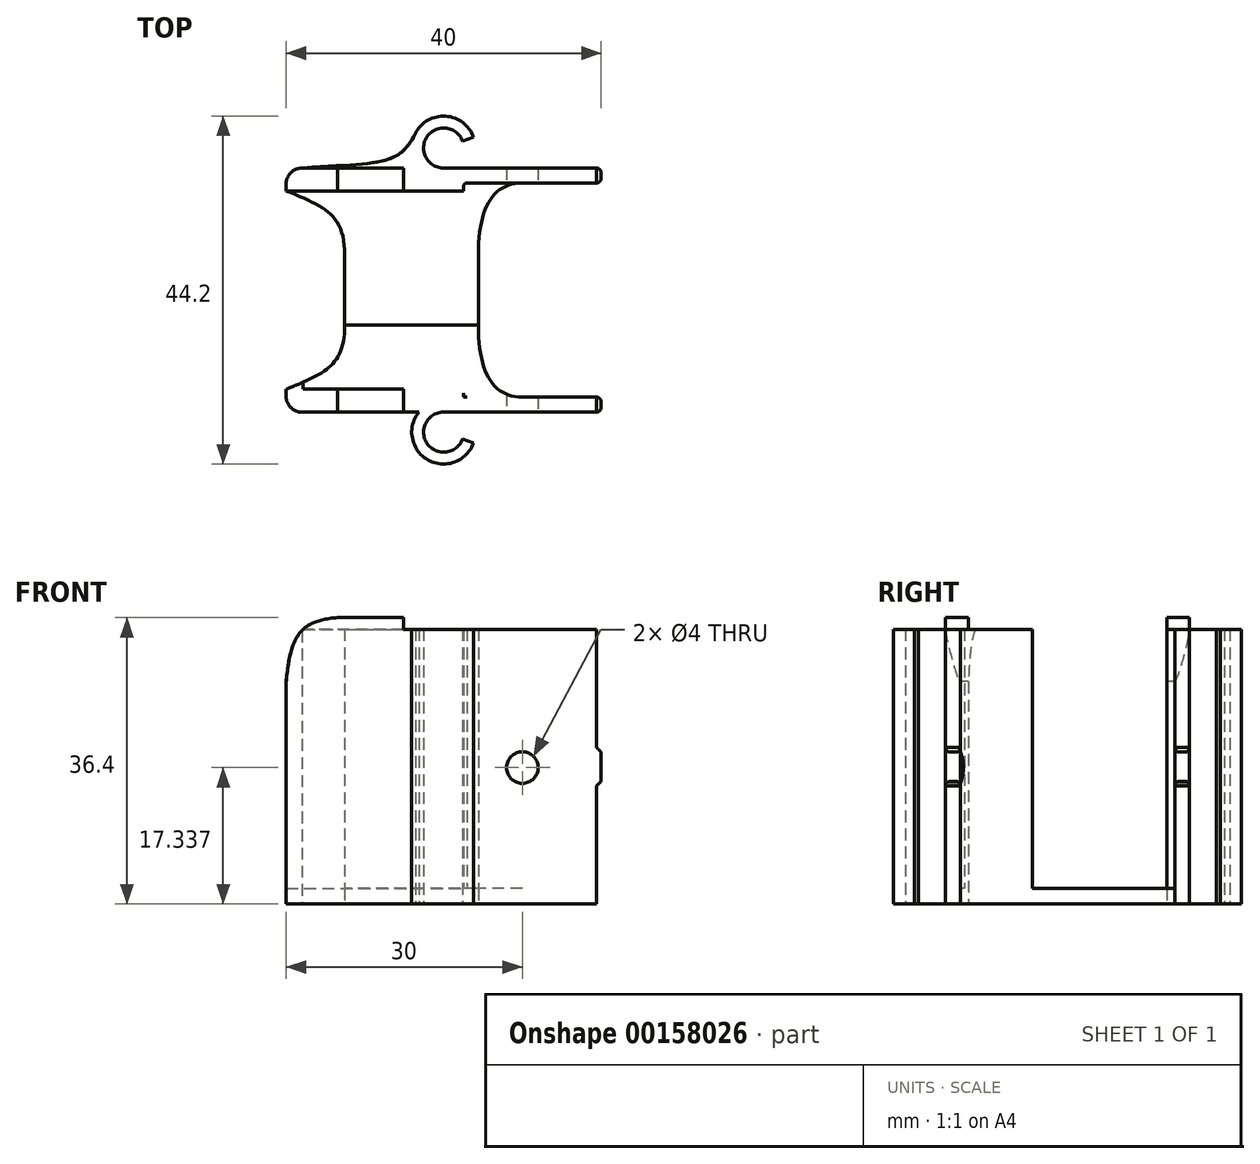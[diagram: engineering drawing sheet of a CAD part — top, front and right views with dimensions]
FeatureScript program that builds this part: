
annotation { "Feature Type Name" : "Feature", "Feature Type Description" : "" }
export const myFeature = defineFeature(function(context is Context, id is Id, definition is map)
    precondition{}
    {
        {
            var Q0;
            Q0=qCreatedBy(makeId("Top.planeOp"),FACE);
            var sketch = newSketch(context, id + "F0", { "sketchPlane" : qUnion([Q0])});
            skCircle(sketch, "E0", {"center": v(0, 18.05) * mm, "radius": 2.55 * mm});
            skCircle(sketch, "E1", {"center": v(0, 18.05) * mm, "radius": 4.05 * mm});
            skLineSegment(sketch, "E2", {"start": v(-20, 12.6) * mm, "end": v(2.5, 12.6) * mm});
            skLineSegment(sketch, "E3", {"start": v(19.4, 15.5) * mm, "end": v(-18, 15.5) * mm});
            skLineSegment(sketch, "E4", {"start": v(-20, 13.5) * mm, "end": v(-20, 12.6) * mm});
            skLineSegment(sketch, "E5", {"start": v(-43.37, 0) * mm, "end": v(27.82, 0) * mm, "construction": true});
            skLineSegment(sketch, "E6", {"start": v(10, 20.96) * mm, "end": v(10, -7.85) * mm, "construction": true});
            skLineSegment(sketch, "E7", {"start": v(0, 18.05) * mm, "end": v(11.1, 22.1) * mm});
            skLineSegment(sketch, "E8", {"start": v(14.32, 18.05) * mm, "end": v(-31, 18.05) * mm, "construction": true});
            skLineSegment(sketch, "E9", {"start": v(20, 14.9) * mm, "end": v(20, 14.2) * mm});
            skLineSegment(sketch, "E10", {"start": v(19.4, 13.6) * mm, "end": v(3, 13.6) * mm});
            skLineSegment(sketch, "E11", {"start": v(2.5, 12.6) * mm, "end": v(2.5, 13.1) * mm});
            skPoint(sketch, "E12.visualSharp", {"position": v(20, 15.5) * mm});
            skArc(sketch, "E12.filletArc", {"start": v(20, 14.9) * mm, "mid": v(19.82, 15.32) * mm, "end": v(19.4, 15.5) * mm});
            skPoint(sketch, "E13.visualSharp", {"position": v(20, 13.6) * mm});
            skArc(sketch, "E13.filletArc", {"start": v(19.4, 13.6) * mm, "mid": v(19.82, 13.78) * mm, "end": v(20, 14.2) * mm});
            skPoint(sketch, "E14.visualSharp", {"position": v(-20, 15.5) * mm});
            skArc(sketch, "E14.filletArc", {"start": v(-18, 15.5) * mm, "mid": v(-19.41, 14.91) * mm, "end": v(-20, 13.5) * mm});
            skLineSegment(sketch, "E15.bottom", {"start": v(-12.56, 0) * mm, "end": v(4.4, 0) * mm});
            skLineSegment(sketch, "E15.top", {"start": v(-12.56, 4.46) * mm, "end": v(4.4, 4.46) * mm});
            skLineSegment(sketch, "E15.left", {"start": v(-12.56, 0) * mm, "end": v(-12.56, 4.46) * mm});
            skLineSegment(sketch, "E15.right", {"start": v(4.4, 0) * mm, "end": v(4.4, 4.46) * mm});
            skLineSegment(sketch, "E16.MirrorCS", {"start": v(20, -14.9) * mm, "end": v(20, -14.2) * mm});
            skArc(sketch, "E17.MirrorCS", {"start": v(19.4, -13.6) * mm, "mid": v(19.82, -13.78) * mm, "end": v(20, -14.2) * mm});
            skArc(sketch, "E18.MirrorCS", {"start": v(20, -14.9) * mm, "mid": v(19.82, -15.32) * mm, "end": v(19.4, -15.5) * mm});
            skLineSegment(sketch, "E19.MirrorCS", {"start": v(2.5, -12.6) * mm, "end": v(2.5, -13.6) * mm});
            skLineSegment(sketch, "E20.MirrorCS", {"start": v(-20, -13.5) * mm, "end": v(-20, -12.6) * mm});
            skArc(sketch, "E21.MirrorCS", {"start": v(-18, -15.5) * mm, "mid": v(-19.41, -14.91) * mm, "end": v(-20, -13.5) * mm});
            skPoint(sketch, "E22.MirrorP", {"position": v(20, -15.5) * mm});
            skLineSegment(sketch, "E23.MirrorCS", {"start": v(19.4, -13.6) * mm, "end": v(2.5, -13.6) * mm});
            skLineSegment(sketch, "E24.MirrorCS", {"start": v(19.4, -15.5) * mm, "end": v(-18, -15.5) * mm});
            skLineSegment(sketch, "E25.MirrorCS", {"start": v(-20, -12.6) * mm, "end": v(2.5, -12.6) * mm});
            skPoint(sketch, "E26.MirrorP", {"position": v(20, -13.6) * mm});
            skCircle(sketch, "E27.MirrorC", {"center": v(0, -18.05) * mm, "radius": 4.05 * mm});
            skCircle(sketch, "E28.MirrorC", {"center": v(0, -18.05) * mm, "radius": 2.55 * mm});
            skPoint(sketch, "E29.MirrorP", {"position": v(-20, -15.5) * mm});
            skLineSegment(sketch, "E30.MirrorCS", {"start": v(-12.56, -4.46) * mm, "end": v(4.4, -4.46) * mm});
            skLineSegment(sketch, "E31.MirrorCS", {"start": v(-12.56, 0) * mm, "end": v(-12.56, -4.46) * mm});
            skLineSegment(sketch, "E32.MirrorCS", {"start": v(4.4, 0) * mm, "end": v(4.4, -4.46) * mm});
            skLineSegment(sketch, "E33.MirrorCS", {"start": v(0, -18.05) * mm, "end": v(11.1, -22.1) * mm});
            skFitSpline(sketch, "E34", {"points": [v(10, 13.6) * mm, v(4.4, 4.46) * mm], "startDerivative": vector(-11.27, 0) * mm, "endDerivative": vector(0, -18.1) * mm});
            skFitSpline(sketch, "E35", {"points": [v(-20, 12.6) * mm, v(-12.56, 4.46) * mm], "startDerivative": vector(13.93, -5.77) * mm, "endDerivative": vector(0, -15.8) * mm});
            skFitSpline(sketch, "E36.MirrorCS", {"points": [v(10, -13.6) * mm, v(4.4, -4.46) * mm], "startDerivative": vector(-11.27, 0) * mm, "endDerivative": vector(0, 18.1) * mm});
            skFitSpline(sketch, "E37.MirrorCS", {"points": [v(-20, -12.6) * mm, v(-12.56, -4.46) * mm], "startDerivative": vector(13.93, 5.77) * mm, "endDerivative": vector(0, 15.8) * mm});
            skPoint(sketch, "E38", {"position": v(-8.34, 18.05) * mm});
            skFitSpline(sketch, "E39", {"points": [v(-18, 15.5) * mm, v(-3.59, 19.93) * mm], "startDerivative": vector(27.98, 2.16) * mm, "endDerivative": vector(6.23, 13.18) * mm});
            skPoint(sketch, "E40.visualSharp", {"position": v(2.5, 13.6) * mm});
            skArc(sketch, "E40.filletArc", {"start": v(3, 13.6) * mm, "mid": v(2.65, 13.45) * mm, "end": v(2.5, 13.1) * mm});
            skArc(sketch, "E41.MirrorCS", {"start": v(3, -13.6) * mm, "mid": v(2.65, -13.45) * mm, "end": v(2.5, -13.1) * mm});
            skFitSpline(sketch, "E42.MirrorCS", {"points": [v(-18, -15.5) * mm, v(-3.59, -19.93) * mm], "startDerivative": vector(27.98, -2.16) * mm, "endDerivative": vector(6.23, -13.18) * mm});
            skLineSegment(sketch, "E43", {"start": v(-5.1, -15.5) * mm, "end": v(-5.1, -12.6) * mm});
            skLineSegment(sketch, "E44.MirrorCS", {"start": v(-5.1, 15.5) * mm, "end": v(-5.1, 12.6) * mm});
            skSolve(sketch);
        }
        {
            var Q0;
            Q0=makeQuery(id+"F0.imprint","IMPRINT",FACE,{"disambiguationData":[TD([[makeQuery(id+"F0.imprint","IMPRINT",EDGE,{"derivedFrom":sQuery(id+"F0.wireOp",EDGE,"E2")}),1.0]])]});
            var Q1;
            {var subQ0=sQuery(id+"F0.wireOp",EDGE,"E3");var subQ1=sQuery(id+"F0.wireOp",EDGE,"E1");var subQ2=makeQuery(id+"F0.imprint","INTERSECT",VERTEX,{"disambiguationData":[OD(0.0)],"derivedFrom":[subQ1,subQ0]});Q1=makeQuery(id+"F0.imprint","IMPRINT",FACE,{"disambiguationData":[TD([[makeQuery(id+"F0.imprint","IMPRINT",EDGE,{"disambiguationData":[TD([[subQ2,1.0]])],"derivedFrom":subQ1}),1.0]])]});}
            var Q2;
            Q2=makeQuery(id+"F0.imprint","IMPRINT",FACE,{"disambiguationData":[TD([[makeQuery(id+"F0.imprint","IMPRINT",EDGE,{"derivedFrom":sQuery(id+"F0.wireOp",EDGE,"E9")}),-1.0]])]});
            extrude(context, id + "F1", {"entities" : qUnion([Q0, Q1, Q2]), "depth" : 34.9 * mm});
        }
        {
            var Q0;
            Q0=makeQuery(id+"F0.imprint","IMPRINT",FACE,{"disambiguationData":[TD([[makeQuery(id+"F0.imprint","IMPRINT",EDGE,{"derivedFrom":sQuery(id+"F0.wireOp",EDGE,"E2")}),-1.0]])]});
            var Q1;
            Q1=makeQuery(id+"F0.imprint","IMPRINT",FACE,{"disambiguationData":[TD([[makeQuery(id+"F0.imprint","IMPRINT",EDGE,{"derivedFrom":sQuery(id+"F0.wireOp",EDGE,"E15.bottom")}),1.0]])]});
            var Q2;
            Q2=makeQuery(id+"F0.imprint","IMPRINT",FACE,{"disambiguationData":[TD([[makeQuery(id+"F0.imprint","IMPRINT",EDGE,{"derivedFrom":sQuery(id+"F0.wireOp",EDGE,"E15.bottom")}),-1.0]])]});
            var Q3;
            Q3=makeQuery(id+"F0.imprint","IMPRINT",FACE,{"disambiguationData":[TD([[makeQuery(id+"F0.imprint","IMPRINT",EDGE,{"derivedFrom":sQuery(id+"F0.wireOp",EDGE,"b0b9aed6-4291-49e0-8eb1-d7c1ce640f5c6.MirrorCS")}),1.0]])]});
            var Q4;
            {var subQ1=sQuery(id+"F0.wireOp",EDGE,"E19.MirrorCS");Q4=makeQuery(id+"F0.imprint","IMPRINT",FACE,{"disambiguationData":[TD([[makeQuery(id+"F0.imprint","IMPRINT",EDGE,{"derivedFrom":subQ1}),1.0]])]});}
            var Q5;
            {var subQ3=sQuery(id+"F0.wireOp",EDGE,"E25.MirrorCS");Q5=makeQuery(id+"F0.imprint","IMPRINT",FACE,{"disambiguationData":[TD([[makeQuery(id+"F0.imprint","IMPRINT",EDGE,{"derivedFrom":subQ3}),1.0]])]});}
            extrude(context, id + "F2", {"entities" : qUnion([Q0, Q1, Q2, Q3, Q4, Q5]), "operationType" : NewBodyOperationType.ADD, "depth" : 2 * mm});
        }
        {
            var Q0;
            Q0=makeQuery(id+"F0.imprint","IMPRINT",FACE,{"disambiguationData":[TD([[makeQuery(id+"F0.imprint","IMPRINT",EDGE,{"derivedFrom":sQuery(id+"F0.wireOp",EDGE,"E16.MirrorCS")}),1.0]])]});
            var Q1;
            {var subQ0=sQuery(id+"F0.wireOp",EDGE,"E27.MirrorC");var subQ1=sQuery(id+"F0.wireOp",EDGE,"E24.MirrorCS");var subQ2=makeQuery(id+"F0.imprint","INTERSECT",VERTEX,{"disambiguationData":[OD(0.0)],"derivedFrom":[subQ1,subQ0]});Q1=makeQuery(id+"F0.imprint","IMPRINT",FACE,{"disambiguationData":[TD([[makeQuery(id+"F0.imprint","IMPRINT",EDGE,{"disambiguationData":[TD([[subQ2,-1.0]])],"derivedFrom":subQ1}),-1.0]])]});}
            var Q2;
            {var subQ3=sQuery(id+"F0.wireOp",EDGE,"E41.MirrorCS");Q2=makeQuery(id+"F0.imprint","IMPRINT",FACE,{"disambiguationData":[TD([[makeQuery(id+"F0.imprint","IMPRINT",EDGE,{"derivedFrom":subQ3}),1.0]])]});}
            var Q3;
            {var subQ1=sQuery(id+"F0.wireOp",EDGE,"E20.MirrorCS");Q3=makeQuery(id+"F0.imprint","IMPRINT",FACE,{"disambiguationData":[TD([[makeQuery(id+"F0.imprint","IMPRINT",EDGE,{"derivedFrom":subQ1}),-1.0]])]});}
            extrude(context, id + "F3", {"entities" : qUnion([Q0, Q1, Q2, Q3]), "operationType" : NewBodyOperationType.ADD, "depth" : 34.9 * mm});
        }
        {
            var Q0;
            {var subQ1=sQuery(id+"F0.wireOp",EDGE,"E20.MirrorCS");Q0=makeQuery(id+"F0.imprint","IMPRINT",FACE,{"disambiguationData":[TD([[makeQuery(id+"F0.imprint","IMPRINT",EDGE,{"derivedFrom":subQ1}),-1.0]])]});}
            var Q1;
            {var subQ0=sQuery(id+"F0.wireOp",EDGE,"E4");Q1=makeQuery(id+"F0.imprint","IMPRINT",FACE,{"disambiguationData":[TD([[makeQuery(id+"F0.imprint","IMPRINT",EDGE,{"derivedFrom":subQ0}),1.0]])]});}
            extrude(context, id + "F4", {"entities" : qUnion([Q0, Q1]), "operationType" : NewBodyOperationType.ADD, "depth" : (34.9 + 1.5) * mm});
        }
        {
            var Q0;
            {var subQ0=sQuery(id+"F0.wireOp",EDGE,"NV3YmyAq-PTGJ-rEJk-GbOK-2QoN2BAdSVcs");Q0=makeQuery(id+"F0.imprint","IMPRINT",FACE,{"disambiguationData":[TD([[makeQuery(id+"F0.imprint","IMPRINT",EDGE,{"derivedFrom":subQ0}),-1.0]])]});}
            var Q1;
            {var subQ1=sQuery(id+"F0.wireOp",EDGE,"E0");var subQ6=sQuery(id+"F0.wireOp",EDGE,"E7");var subQ8=makeQuery(id+"F0.imprint","INTERSECT",VERTEX,{"derivedFrom":[subQ1,subQ6]});Q1=makeQuery(id+"F0.imprint","IMPRINT",FACE,{"disambiguationData":[TD([[makeQuery(id+"F0.imprint","IMPRINT",EDGE,{"disambiguationData":[TD([[subQ8,-1.0]])],"derivedFrom":subQ1}),-1.0]])]});}
            var Q2;
            {var subQ0=sQuery(id+"F0.wireOp",EDGE,"E170.MirrorCS");Q2=makeQuery(id+"F0.imprint","IMPRINT",FACE,{"disambiguationData":[TD([[makeQuery(id+"F0.imprint","IMPRINT",EDGE,{"derivedFrom":subQ0}),1.0]])]});}
            var Q3;
            {var subQ1=sQuery(id+"F0.wireOp",EDGE,"E28.MirrorC");var subQ3=sQuery(id+"F0.wireOp",EDGE,"E24.MirrorCS");var subQ4=makeQuery(id+"F0.imprint","INTERSECT",VERTEX,{"derivedFrom":[subQ3,subQ1]});Q3=makeQuery(id+"F0.imprint","IMPRINT",FACE,{"disambiguationData":[TD([[makeQuery(id+"F0.imprint","IMPRINT",EDGE,{"disambiguationData":[TD([[subQ4,-1.0]])],"derivedFrom":subQ3}),1.0]])]});}
            var Q4;
            {var subQ0=sQuery(id+"F0.wireOp",EDGE,"E42.MirrorCS");var subQ3=sQuery(id+"F0.wireOp",EDGE,"E27.MirrorC");var subQ5=makeQuery(id+"F0.imprint","INTERSECT",VERTEX,{"disambiguationData":[OD(1.0)],"derivedFrom":[subQ3,subQ0]});Q4=makeQuery(id+"F0.imprint","IMPRINT",FACE,{"disambiguationData":[TD([[makeQuery(id+"F0.imprint","IMPRINT",EDGE,{"disambiguationData":[TD([[subQ5,-1.0]])],"derivedFrom":subQ3}),1.0]])]});}
            var Q5;
            {var subQ0=sQuery(id+"F0.wireOp",EDGE,"E39");var subQ1=sQuery(id+"F0.wireOp",EDGE,"E1");var subQ2=makeQuery(id+"F0.imprint","INTERSECT",VERTEX,{"disambiguationData":[OD(1.0)],"derivedFrom":[subQ1,subQ0]});Q5=makeQuery(id+"F0.imprint","IMPRINT",FACE,{"disambiguationData":[TD([[makeQuery(id+"F0.imprint","IMPRINT",EDGE,{"disambiguationData":[TD([[subQ2,-1.0]])],"derivedFrom":subQ1}),-1.0]])]});}
            extrude(context, id + "F5", {"entities" : qUnion([Q0, Q1, Q2, Q3, Q4, Q5]), "operationType" : NewBodyOperationType.ADD, "depth" : 34.9 * mm});
        }
        {
            var Q0;
            Q0=makeQuery(id+"F3.opExtrude","SWEPT_FACE",FACE,{"disambiguationData":[OSD([sQuery(id+"F0.wireOp",EDGE,"E24.MirrorCS")])]});
            var sketch = newSketch(context, id + "F6", { "sketchPlane" : qUnion([Q0])});
            skPoint(sketch, "E45", {"position": v(-18, 17.79) * mm});
            skLineSegment(sketch, "E46", {"start": v(-29.53, 17.79) * mm, "end": v(34.17, 17.06) * mm, "construction": true});
            skCircle(sketch, "E47", {"center": v(10, 17.34) * mm, "radius": 2 * mm});
            skLineSegment(sketch, "E48.0", {"start": v(0, 34.9) * mm, "end": v(0, 0) * mm});
            skPoint(sketch, "E49", {"position": v(0, 17.45) * mm});
            skSolve(sketch);
        }
        {
            var Q0;
            Q0 = qSketchRegion(id + "F6", true);
            extrude(context, id + "F7", {"entities" : qUnion([Q0]), "operationType" : NewBodyOperationType.REMOVE, "endBound" : BoundingType.THROUGH_ALL, "oppositeDirection" : true, "depth" : 25 * mm});
        }
        {
            var Q0;
            Q0=makeQuery(id+"F6.imprint","IMPRINT",FACE,{"disambiguationData":[TD([[makeQuery(id+"F6.imprint","IMPRINT",EDGE,{"derivedFrom":sQuery(id+"F6.wireOp",EDGE,"E47")}),-1.0]])]});
            var sketch = newSketch(context, id + "F8", { "sketchPlane" : qUnion([Q0])});
            skLineSegment(sketch, "E50.0", {"start": v(19.4, 34.9) * mm, "end": v(0, 34.9) * mm});
            skLineSegment(sketch, "E51.0", {"start": v(19.4, 0) * mm, "end": v(-18, 0) * mm});
            skLineSegment(sketch, "E52", {"start": v(2.5, 34.9) * mm, "end": v(20, 34.9) * mm});
            skLineSegment(sketch, "E53", {"start": v(2.5, 0) * mm, "end": v(20, 0) * mm});
            skPoint(sketch, "E54", {"position": v(20, 17.45) * mm});
            skLineSegment(sketch, "E55.0", {"start": v(4.4, 2) * mm, "end": v(4.4, 0) * mm});
            skLineSegment(sketch, "E56", {"start": v(4.4, 0) * mm, "end": v(20, 15.6) * mm});
            skLineSegment(sketch, "E57", {"start": v(4.4, 34.9) * mm, "end": v(20, 19.3) * mm});
            skLineSegment(sketch, "E58.0", {"start": v(20, 34.9) * mm, "end": v(20, 0) * mm});
            skLineSegment(sketch, "E59.0", {"start": v(-5.1, 36.4) * mm, "end": v(-18, 36.4) * mm});
            skLineSegment(sketch, "E60", {"start": v(-13.47, 36.4) * mm, "end": v(-20, 36.4) * mm});
            skLineSegment(sketch, "E61", {"start": v(-20, 36.4) * mm, "end": v(-20, 28.26) * mm});
            skFitSpline(sketch, "E62", {"points": [v(-20, 28.26) * mm, v(-13.47, 36.4) * mm], "startDerivative": vector(1.65, 18.53) * mm, "endDerivative": vector(13.61, 1.15) * mm});
            skLineSegment(sketch, "E63.0", {"start": v(-20, 36.4) * mm, "end": v(-20, 0) * mm});
            skSolve(sketch);
        }
        {
            var Q0;
            {var subQ0=sQuery(id+"F8.wireOp",EDGE,"944b5dbf-c12b-4d65-9681-d408ed4463f3.0");var subQ1=sQuery(id+"F8.wireOp",EDGE,"c34d9e39-a528-4fdd-849f-dd87dd5dee8a.0");var subQ2=makeQuery(id+"F8.imprint","INTERSECT",VERTEX,{"derivedFrom":[subQ1,subQ0]});Q0=makeQuery(id+"F8.imprint","IMPRINT",FACE,{"disambiguationData":[TD([[makeQuery(id+"F8.imprint","IMPRINT",EDGE,{"disambiguationData":[TD([[subQ2,-1.0]])],"derivedFrom":subQ1}),-1.0]])]});}
            var Q1;
            {var subQ0=sQuery(id+"F8.wireOp",EDGE,"E52");var subQ3=sQuery(id+"F8.wireOp",EDGE,"E57");var subQ4=makeQuery(id+"F8.imprint","INTERSECT",VERTEX,{"derivedFrom":[subQ0,subQ3]});Q1=makeQuery(id+"F8.imprint","IMPRINT",FACE,{"disambiguationData":[TD([[makeQuery(id+"F8.imprint","IMPRINT",EDGE,{"disambiguationData":[TD([[subQ4,1.0]])],"derivedFrom":subQ0}),1.0]])]});}
            var Q2;
            {var subQ0=sQuery(id+"F8.wireOp",EDGE,"E52");var subQ3=sQuery(id+"F8.wireOp",EDGE,"E58.0");var subQ4=makeQuery(id+"F8.imprint","INTERSECT",VERTEX,{"derivedFrom":[subQ0,subQ3]});Q2=makeQuery(id+"F8.imprint","IMPRINT",FACE,{"disambiguationData":[TD([[makeQuery(id+"F8.imprint","IMPRINT",EDGE,{"disambiguationData":[TD([[subQ4,-1.0]])],"derivedFrom":subQ3}),-1.0]])]});}
            var Q3;
            {var subQ0=sQuery(id+"F8.wireOp",EDGE,"E53");var subQ3=sQuery(id+"F8.wireOp",EDGE,"E56");var subQ4=makeQuery(id+"F8.imprint","INTERSECT",VERTEX,{"derivedFrom":[subQ0,subQ3]});Q3=makeQuery(id+"F8.imprint","IMPRINT",FACE,{"disambiguationData":[TD([[makeQuery(id+"F8.imprint","IMPRINT",EDGE,{"disambiguationData":[TD([[subQ4,1.0]])],"derivedFrom":subQ0}),-1.0]])]});}
            var Q4;
            {var subQ0=sQuery(id+"F8.wireOp",EDGE,"E53");var subQ3=sQuery(id+"F8.wireOp",EDGE,"E58.0");var subQ4=makeQuery(id+"F8.imprint","INTERSECT",VERTEX,{"derivedFrom":[subQ0,subQ3]});Q4=makeQuery(id+"F8.imprint","IMPRINT",FACE,{"disambiguationData":[TD([[makeQuery(id+"F8.imprint","IMPRINT",EDGE,{"disambiguationData":[TD([[subQ4,1.0]])],"derivedFrom":subQ3}),-1.0]])]});}
            var Q5;
            {var subQ0=sQuery(id+"F8.wireOp",EDGE,"E62");Q5=makeQuery(id+"F8.imprint","IMPRINT",FACE,{"disambiguationData":[TD([[makeQuery(id+"F8.imprint","IMPRINT",EDGE,{"derivedFrom":subQ0}),1.0]])]});}
            extrude(context, id + "F9", {"entities" : qUnion([Q0, Q1, Q2, Q3, Q4, Q5]), "operationType" : NewBodyOperationType.REMOVE, "endBound" : BoundingType.SYMMETRIC, "oppositeDirection" : true, "depth" : 84 * mm});
        }
    });
